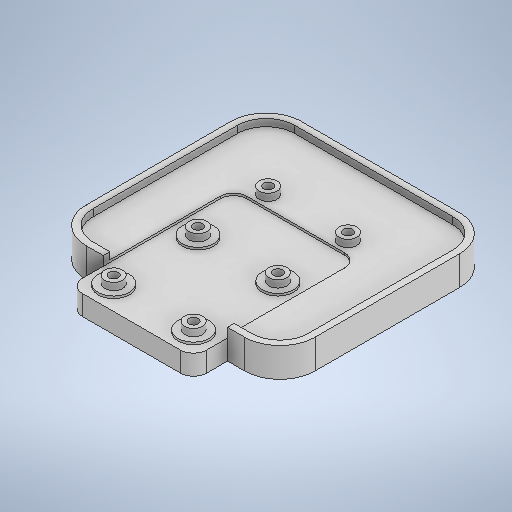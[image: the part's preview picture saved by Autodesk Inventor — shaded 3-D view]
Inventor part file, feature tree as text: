
AUTODESK INVENTOR PART (.ipt)
format: ipt  version: 2025 (Build 290162000, 162)  size: 403,968 bytes
history: native  units: mm
features: extrude x5, sketch x5, projected_geometry x2, shell x1
ambient origin geometry x8: Origin, YZ Plane, XZ Plane, XY Plane, X Axis, Y Axis, Z Axis, Center Point
bodies: Solid1 (feature_tree)
feature tree (13):
  extrude  "Extrusion1"  Depth=51.6mm
  shell  "Shell1"  Thickness=7.65mm
  extrude  "Extrusion2"  Depth=3.0mm
  extrude  "Extrusion3"  Depth=1.5mm
  extrude  "Extrusion4"  Depth=2.1mm
  extrude  "Extrusion5"  Depth=37.0mm
  sketch  "Sketch1"  dims[d0=48.5mm d1=51.6mm d2=7.65mm]
  sketch  "Sketch2"  dims[d3=28.0mm d5=3.0mm]
  sketch  "Sketch3"  dims[d6=5.0mm d7=0.0mm d8=1.5mm]
  sketch  "Sketch4"  dims[d10=8.0mm d11=2.1mm]
  sketch  "Sketch5"  dims[d12=18.0mm d13=15.8mm d14=19.0mm d15=0.0mm d16=0.0mm d17=1.5mm d18=1.6mm d19=0.0mm d20=4.0mm d21=1.6mm d22=0.0mm d25=7.0mm d26=0.5mm d27=0.0mm d29=37.0mm]
  projected_geometry  "Project Cut Edges1"
  projected_geometry  "Project Cut Edges2"
